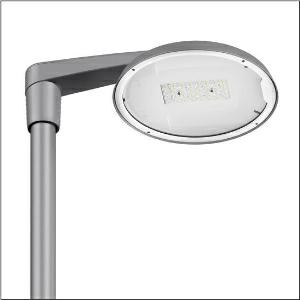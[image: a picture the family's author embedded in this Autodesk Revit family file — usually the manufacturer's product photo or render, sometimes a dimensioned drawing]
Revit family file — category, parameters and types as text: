
# Revit family: dl_50_iq_mini___st0_5a_5xa248b41f08fe_6912
name_source: partatom
category: Lighting Fixtures
units: mm (PartAtom-declared; Revit-internal decimal feet)

## family parameters
Cut with Voids When Loaded = No
Host = Face
Light Source = No
Part Type = Normal
Room Calculation Point = No
Round Connector Dimension = Use Diameter
Shared = No

## types (1)
- --- (1 x LED, 2690 lm, 15.7 W, 4000K)
    Apparent Load = 16 VA
    CIE Flux Codes = 41 75 97 100 100
    Color Rendering = 70
    Color Temperature = 4000K
    Default Elevation = 1800 mm
    Description = DL 50 iQ mini, mast luminaire, primary light control with lens, of PMMA, primary optical cover: cover, of toughened safety glass, transparent, light distribution: ST0.5a, light emission: direct distribution, primary light characteristic: asymmetric, installation type: side-entry, post-top, LED, High Power LED, rated luminous flux: 2.690lm, luminous efficacy: 171lm/W, light colour: 740, colour temperature: 4000K, control gear: iQ Street-Remote, control: optimised constant luminous flux control (CLO 2.0), Desk-Remote (wireless, voltage-free reading and setting of iQ features in the workshop via application-optimized NFC function/RFID function), Light-Fading, Smart-Wire, Night-Set, Lumen-Switch, Temp-Guard, Auto-Match, Street-Remote, mains connection: 230..240V, AC, 50/60Hz, connection cable pre-assembled, cable length: 6,5m, start of lifetime: 16W, end of service life: 16W, reduction: 8W, luminaire housing, of diecast aluminium, powder-coated, SITECO metallic grey (DB 702S), inclination adjustable: 0°, 5°, 10° (post-top) | 0°, -5°, -10°, -15° (side-entry), please order mast post-top element or mast side-entry element separately, diameter: 500mm, height: 115mm, post-top: for spigot size d x l = 76 x 100mm; with reducer (optional accessory) 60 x 100mm | side-entry: for spigot size d x l = 60 x 100mm; with reducer (optional accessory) 42 x 100mm, mounting height: 4..6m, protection rating (complete): IP66, insulation class (complete): insulation class II (safety insulation), certification: CE, ENEC, ENEC+, VDE, impact resistance: IK08, permissible operating ambient temperature for outdoor applications: -25..+40°C, standard-compliant lighting for roads and squares, packaging unit: 1 piece

Light Distribution: ST0.5a
    Height = 115 mm
    Lamp = 1 x LED
    Lamp Light Flux = 2690 lm
    Lamp Power = 15.7 W
    Lamp count = 1
    Length = 500 mm
    Luminous efficacy = 171 lm/W
    Manufacturer = Siteco
    ModVariant = No
    Model = 5XA248B41F08FE
    Number of Poles = 1
    OnlyDefault = Yes
    Power Factor = 1
    Product Name = DL 50 iQ mini | ST0.5a
    Product group = mast luminaire | pylon top
    ProductGroupID = 6100
    Protection Class = Protection class II
    Protection Degree = IP 66
    RLX_Detail_Level = 1
    RLX_Emergency_Light_Flux = 0 lm
    RLX_Emergency_Type = 0
    RLX_Emergency_Type_DB = No
    RlxData = <blob elided: 126757 chars, md5=32d7a126>
    Socket = socket
    Standby Power = 0 W
    System Light Flux = 2690 lm
    System Power = 16 W
    Type Comments = factory setting: luminous flux: 100 % | dim-lin: 254 | 319 mA
    Type Image = l_1251794.jpg
    URL = http://relux.com
    VarID = @adj_138811
    Voltage = 0 V
    Weight = 0.00 kg
    Width = 0 mm  [stored 0 ft]

note: [stored X ft] marks values corroborated as IEEE doubles in the binary element streams (Revit-internal decimal feet)

## geometry (parser evidence)
native form markers: Blend x4, Sweep x11
no freeform markers — native parametric forms only
